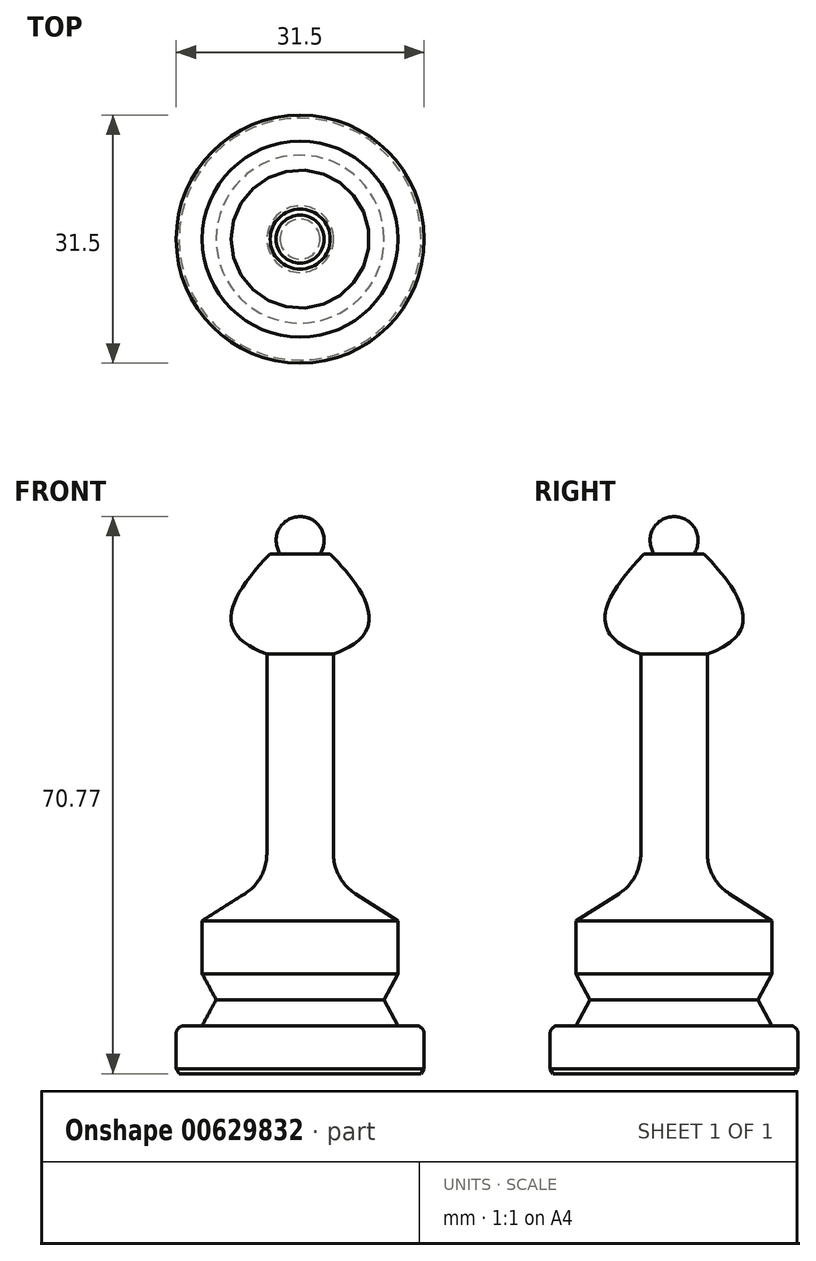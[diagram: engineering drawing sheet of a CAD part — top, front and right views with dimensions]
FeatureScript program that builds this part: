
annotation { "Feature Type Name" : "Feature", "Feature Type Description" : "" }
export const myFeature = defineFeature(function(context is Context, id is Id, definition is map)
    precondition{}
    {
        {
            var Q0;
            Q0=qCreatedBy(makeId("Front.planeOp"),FACE);
            var sketch = newSketch(context, id + "F0", { "sketchPlane" : qUnion([Q0])});
            skLineSegment(sketch, "E0.MirrorCS", {"start": v(15.37, 0) * mm, "end": v(15.75, 0.63) * mm});
            skLineSegment(sketch, "E1.MirrorCS", {"start": v(15.37, 0) * mm, "end": v(0, 0) * mm});
            skLineSegment(sketch, "E2", {"start": v(15.75, 0.64) * mm, "end": v(15.75, 5.08) * mm});
            skArc(sketch, "E3", {"start": v(15.75, 5.08) * mm, "mid": v(15.45, 5.8) * mm, "end": v(14.73, 6.1) * mm});
            skLineSegment(sketch, "E4", {"start": v(14.73, 6.1) * mm, "end": v(12.45, 6.1) * mm});
            skLineSegment(sketch, "E5", {"start": v(12.45, 12.7) * mm, "end": v(12.45, 19.43) * mm});
            skLineSegment(sketch, "E6", {"start": v(12.45, 12.7) * mm, "end": v(10.67, 9.4) * mm});
            skLineSegment(sketch, "E7", {"start": v(10.67, 9.4) * mm, "end": v(12.45, 6.1) * mm});
            skLineSegment(sketch, "E8", {"start": v(12.45, 19.43) * mm, "end": v(7.03, 22.86) * mm});
            skLineSegment(sketch, "E9", {"start": v(4.23, 27.94) * mm, "end": v(4.23, 53.34) * mm});
            skArc(sketch, "E10", {"start": v(4.23, 27.94) * mm, "mid": v(4.98, 25.04) * mm, "end": v(7.03, 22.86) * mm});
            skFitSpline(sketch, "E11", {"points": [v(4.23, 53.34) * mm, v(3.81, 66.04) * mm], "startDerivative": vector(20.8, 7.02) * mm, "endDerivative": vector(-16.95, 17.5) * mm});
            skLineSegment(sketch, "E12", {"start": v(0, 0) * mm, "end": v(0, 66.04) * mm});
            skArc(sketch, "E13", {"start": v(2.54, 66.04) * mm, "mid": v(2.69, 69.17) * mm, "end": v(0, 70.77) * mm});
            skLineSegment(sketch, "E14", {"start": v(2.54, 66.04) * mm, "end": v(3.81, 66.04) * mm});
            skLineSegment(sketch, "E15", {"start": v(0, 66.04) * mm, "end": v(0, 70.77) * mm});
            skSolve(sketch);
        }
        {
            var Q0;
            Q0=makeQuery(id+"F0.imprint","IMPRINT",FACE,{"disambiguationData":[TD([[makeQuery(id+"F0.imprint","IMPRINT",EDGE,{"derivedFrom":sQuery(id+"F0.wireOp",EDGE,"E0.MirrorCS")}),1.0]])]});
            var Q1;
            Q1=sQuery(id+"F0.wireOp",EDGE,"E12");
            revolve(context, id + "F1", {"entities" : qUnion([Q0]), "axis" : qUnion([Q1]), "revolveType" : RevolveType.FULL});
        }
    });
